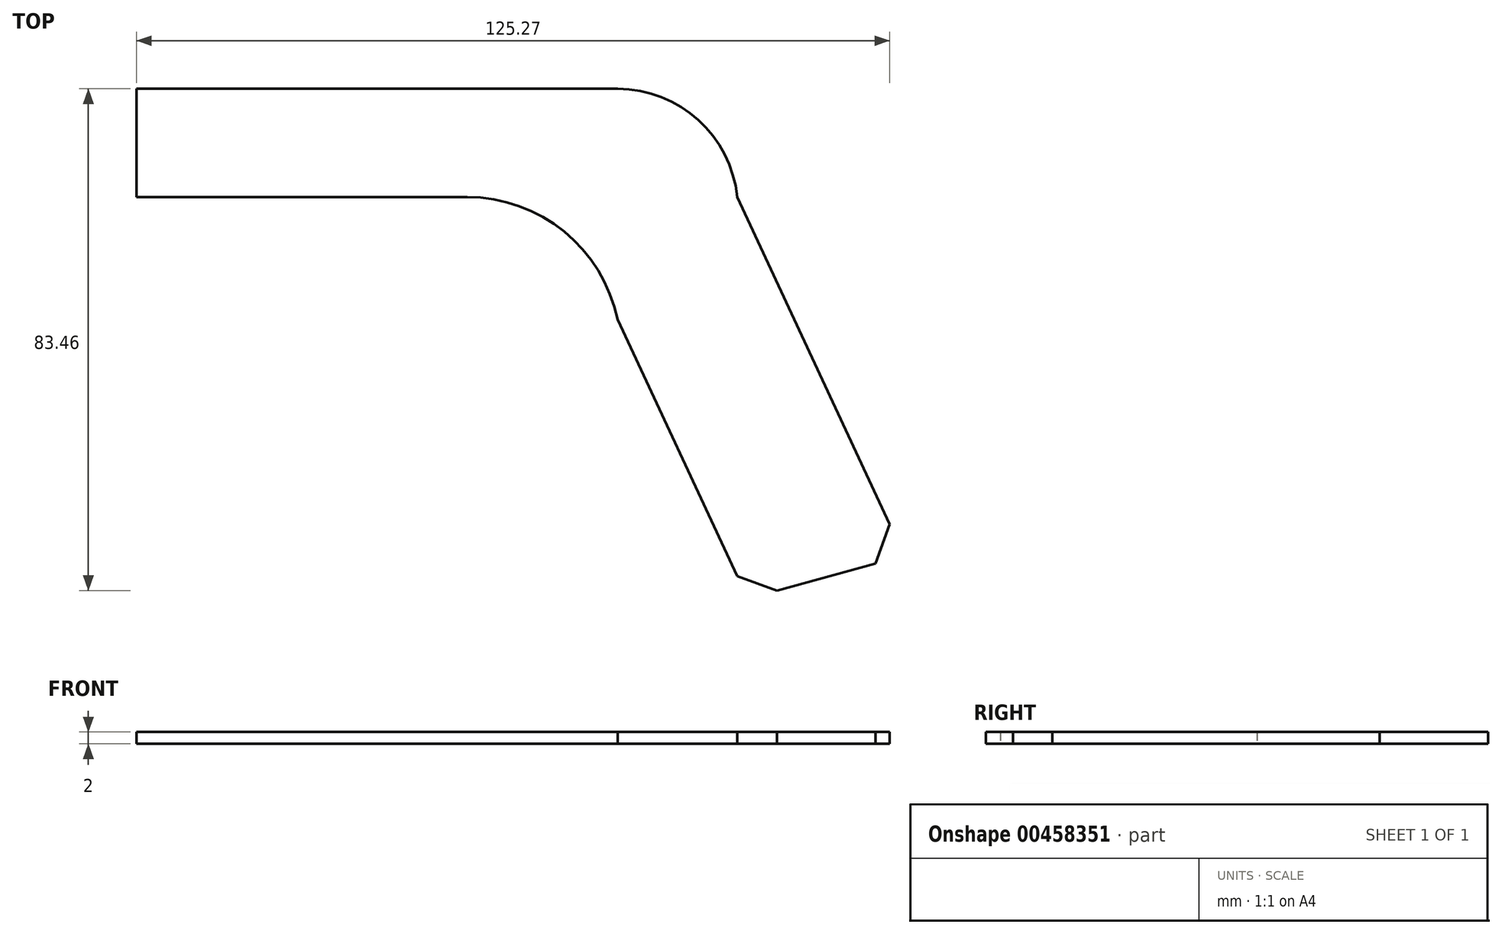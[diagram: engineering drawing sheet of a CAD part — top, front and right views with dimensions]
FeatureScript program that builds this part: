
annotation { "Feature Type Name" : "Feature", "Feature Type Description" : "" }
export const myFeature = defineFeature(function(context is Context, id is Id, definition is map)
    precondition{}
    {
        {
            var Q0;
            Q0=qCreatedBy(makeId("Top.planeOp"),FACE);
            var sketch = newSketch(context, id + "F0", { "sketchPlane" : qUnion([Q0])});
            skLineSegment(sketch, "E0", {"start": v(-62, 18) * mm, "end": v(18, 18) * mm});
            skLineSegment(sketch, "E1", {"start": v(37.9, 0) * mm, "end": v(63.27, -54.41) * mm});
            skLineSegment(sketch, "E2", {"start": v(63.27, -54.41) * mm, "end": v(60.88, -60.99) * mm});
            skLineSegment(sketch, "E3", {"start": v(44.48, -65.46) * mm, "end": v(37.9, -63.07) * mm});
            skLineSegment(sketch, "E4", {"start": v(37.9, -63.07) * mm, "end": v(18, -20.4) * mm});
            skLineSegment(sketch, "E5", {"start": v(-7, 0) * mm, "end": v(-62, 0) * mm});
            skLineSegment(sketch, "E6", {"start": v(-62, 0) * mm, "end": v(-62, 18) * mm});
            skArc(sketch, "E7", {"start": v(37.9, 0) * mm, "mid": v(31.42, 12.83) * mm, "end": v(18, 18) * mm});
            skLineSegment(sketch, "E8", {"start": v(44.48, -65.46) * mm, "end": v(60.88, -60.99) * mm});
            skArc(sketch, "E9", {"start": v(18, -20.4) * mm, "mid": v(9.13, -5.75) * mm, "end": v(-7, 0) * mm});
            skSolve(sketch);
        }
        {
            var Q0;
            Q0 = qSketchRegion(id + "F0", true);
            extrude(context, id + "F1", {"entities" : qUnion([Q0]), "depth" : 2 * mm});
        }
    });
